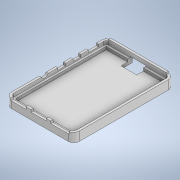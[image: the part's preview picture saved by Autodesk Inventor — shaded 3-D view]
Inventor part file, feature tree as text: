
AUTODESK INVENTOR PART (.ipt)
format: ipt  version: 2022 (Build 260153000, 153)  size: 256,512 bytes
history: native  units: in
note: dims shown in document units (in); Inventor stores cm internally (conversion verified against a paired STEP export)
features: extrude x7, sketch x7
ambient origin geometry x8: Origin, YZ Plane, XZ Plane, XY Plane, X Axis, Y Axis, Z Axis, Center Point
bodies: Solid1 (feature_tree)
feature tree (14):
  extrude  "Extrusion1"  Depth=3.3661in
  extrude  "Extrusion2"  Depth=0.1181in
  extrude  "Extrusion3"  Depth=0.1181in TaperAngle=0.0deg
  extrude  "Extrusion4"  Depth=0.0591in
  extrude  "Extrusion5"  Depth=0.1575in
  extrude  "Extrusion6"  Depth=0.5512in
  extrude  "Extrusion7"  Depth=0.2362in
  sketch  "Sketch1"  dims[d0=2.2244in d1=3.3661in]
  sketch  "Sketch2"  dims[d2=0.0787in d3=0.1181in]
  sketch  "Sketch3"  dims[d4=0.0787in d5=0.1181in d6=0.0in]
  sketch  "Sketch4"  dims[d7=0.0984in d8=0.0in d9=0.0591in]
  sketch  "Sketch5"  dims[d10=0.0787in d11=0.0in d12=0.1575in]
  sketch  "Sketch6"  dims[d13=0.0984in d14=0.0in d16=0.5512in]
  sketch  "Sketch7"  dims[d17=0.0in d18=0.2362in d19=0.3937in d20=0.0in d21=0.2626in d22=0.3619in d23=0.8964in d25=0.2665in d26=0.2665in d27=1.431in d28=2.0399in d29=0.2362in d30=0.0787in d31=0.3937in d32=0.0in d33=0.0787in d34=0.0898in d35=0.5354in d36=0.8048in d37=0.5354in d38=1.4952in d39=0.6442in d40=0.1969in d41=0.0in]
